# Revit family: SANINDUSA_109930004_Hi-dden_66x44Hi-ddenVesselBasin66x44_V0
name_source: partatom
category: Plumbing Fixtures
units: mm (PartAtom-declared; Revit-internal decimal feet)

## family parameters
Cut with Voids When Loaded = No
Host = Face
Part Type = Normal
Room Calculation Point = No
Round Connector Dimension = Use Diameter
Shared = No

## types (1)
- SANINDUSA_109930004_Hi-dden_66x44Hi-ddenVesselBasin66x44_V0
    AssetType = Fixed
    CodePerformance = EN 14688:2006  CL 00
    Color = white
    Default Elevation = 1219 mm
    Description = Waste water appliance for washing the upper parts of the body.
    DrainSize = 45 mm  [stored 0.147638 ft]
    Element Type = WASHHANDBASIN: Waste water appliance for washing the upper parts of the body.
    Features = "Installation on top of furniture. Without overflow."
    Finish = gloss
    Installation Instructions = https://www.tec.sanindusa.pt
    Manufacturer = Sanindusa
    ManufacturerName = Sanindusa
    ManufacturerURL = www.tec.sanindusa.pt
    Material = vitreous china
    Model = 109930004
    ModelNumber = 109930004
    ModelReference = Hi-dden
    Name = 66x44 Hi-dden vessel basin
    NominalDepth = 109 mm  [stored 0.357612 ft]
    NominalHeight = 135 mm  [stored 0.442913 ft]
    NominalLength = 660 mm
    NominalWidth = 437 mm  [stored 1.43373 ft]
    Pre-defined type (IFC) = WASHHANDBASIN
    ProductInformation = https://www.tec.sanindusa.pt
    ProductionYear = 2013
    Size = 66x44
    Type (IFC) = IfcSanitaryTerminalType
    URL = www.tec.sanindusa.pt
    Version = 1
    WarrantyDescription = https://www.tec.sanindusa.pt
    WarrantyDurationParts = 5
    WarrantyDurationUnit = year
    WashHandBasinMounting = countertop
    WashHandBasinType = handrinse
    Waste Connection = Yes
    Weight = 16.70 kg

note: [stored X ft] marks values corroborated as IEEE doubles in the binary element streams (Revit-internal decimal feet)

## geometry (parser evidence)
native form markers: Sweep x8
no freeform markers — native parametric forms only
